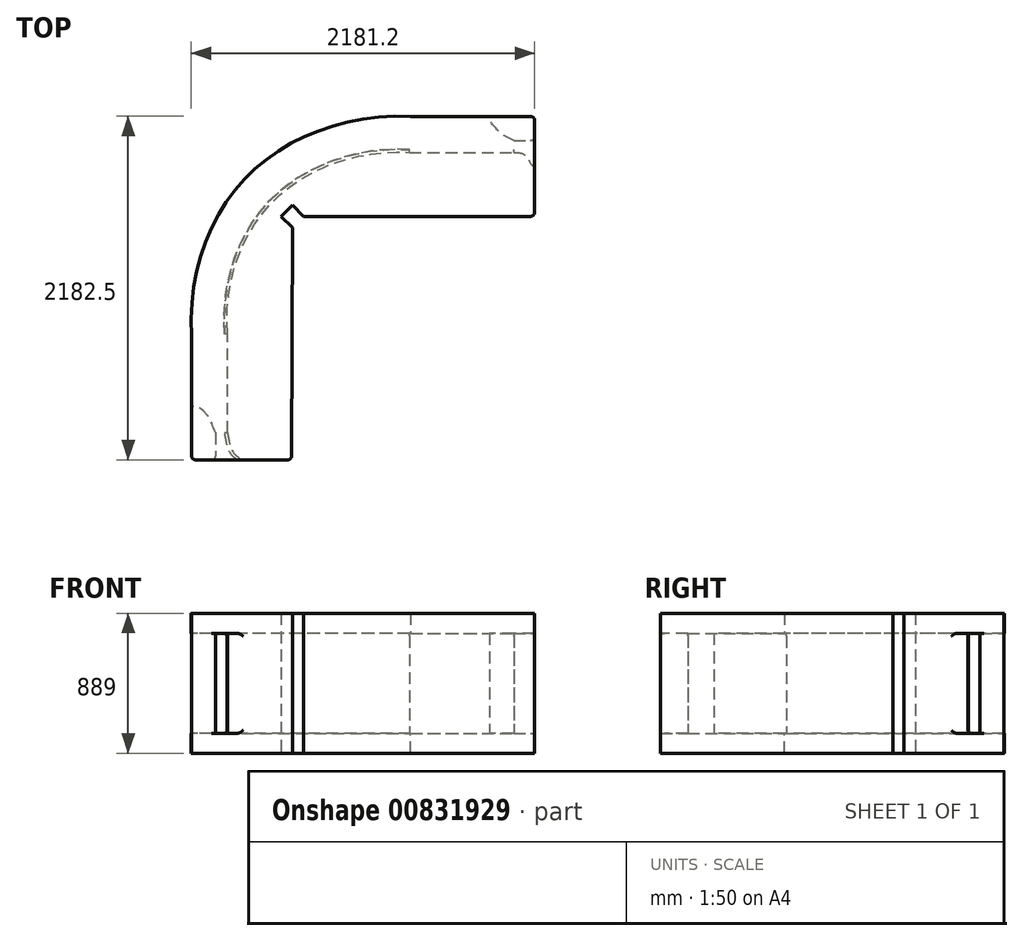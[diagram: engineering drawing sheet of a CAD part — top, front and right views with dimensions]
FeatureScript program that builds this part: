
annotation { "Feature Type Name" : "Feature", "Feature Type Description" : "" }
export const myFeature = defineFeature(function(context is Context, id is Id, definition is map)
    precondition{}
    {
        {
            var Q0;
            Q0=qCreatedBy(makeId("Top.planeOp"),FACE);
            var sketch = newSketch(context, id + "F0", { "sketchPlane" : qUnion([Q0])});
            skFitSpline(sketch, "E0", {"points": [v(690.67, 695.24) * mm, v(-328.68, 333.13) * mm, v(-700.43, -698.84) * mm], "startDerivative": vector(-2366.76, 83.62) * mm, "endDerivative": vector(144.45, -2458.95) * mm});
            skLineSegment(sketch, "E1.top", {"start": v(-700.43, -1486.24) * mm, "end": v(-548.3, -1486.24) * mm});
            skLineSegment(sketch, "E1.left", {"start": v(-700.43, -698.84) * mm, "end": v(-700.43, -1486.24) * mm});
            skLineSegment(sketch, "E2", {"start": v(690.67, 695.24) * mm, "end": v(1478.07, 695.24) * mm});
            skLineSegment(sketch, "E3", {"start": v(1478.07, 695.24) * mm, "end": v(1478.07, 542.84) * mm});
            skLineSegment(sketch, "E4", {"start": v(1478.07, 60.24) * mm, "end": v(11.22, 60.24) * mm});
            skLineSegment(sketch, "E5", {"start": v(11.22, 60.24) * mm, "end": v(-60.63, 132.08) * mm});
            skLineSegment(sketch, "E6", {"start": v(-60.63, 132.08) * mm, "end": v(-132.47, 60.24) * mm});
            skLineSegment(sketch, "E7", {"start": v(-132.47, 60.24) * mm, "end": v(-60.63, -11.6) * mm});
            skFitSpline(sketch, "E8.0", {"points": [v(685.29, 542.94) * mm, v(640.55, 544.52) * mm, v(551.83, 543.62) * mm, v(422.12, 530.41) * mm, v(296.88, 505.7) * mm, v(177.19, 469.84) * mm, v(82.92, 431.02) * mm, v(11.29, 394.8) * mm, v(-40.43, 365.12) * mm, v(-90.04, 332.94) * mm, v(-129.54, 304.1) * mm, v(-159.98, 279.84) * mm, v(-182.21, 261.04) * mm, v(-200.24, 244.9) * mm, v(-214.36, 231.68) * mm, v(-224.8, 221.62) * mm, v(-235.08, 211.4) * mm, v(-248.6, 197.59) * mm, v(-265.13, 179.92) * mm, v(-284.39, 158.12) * mm, v(-309.26, 128.25) * mm, v(-338.84, 89.45) * mm, v(-371.85, 40.62) * mm, v(-402.33, -10.4) * mm, v(-439.47, -81.22) * mm, v(-479.2, -174.78) * mm, v(-515.55, -294.36) * mm, v(-539.97, -420.49) * mm, v(-551.86, -552.38) * mm, v(-551.01, -643.6) * mm, v(-548.3, -689.9) * mm]});
            skPoint(sketch, "E9.end.orphan", {"position": v(1478.07, 542.84) * mm});
            skLineSegment(sketch, "E10", {"start": v(685.28, 542.94) * mm, "end": v(1478.07, 542.84) * mm});
            skLineSegment(sketch, "E11", {"start": v(-548.3, -689.9) * mm, "end": v(-548.3, -1486.24) * mm});
            skFitSpline(sketch, "E12.0", {"points": [v(682.6, 466.78) * mm, v(640.14, 468.28) * mm, v(556.03, 467.43) * mm, v(433.32, 454.93) * mm, v(315.16, 431.6) * mm, v(202.62, 397.88) * mm, v(114.33, 361.5) * mm, v(47.46, 327.7) * mm, v(-0.72, 300.04) * mm, v(-46.83, 270.14) * mm, v(-83.45, 243.4) * mm, v(-111.62, 220.93) * mm, v(-132.19, 203.55) * mm, v(-148.85, 188.63) * mm, v(-161.88, 176.43) * mm, v(-171.5, 167.15) * mm, v(-181, 157.73) * mm, v(-193.48, 144.97) * mm, v(-208.74, 128.66) * mm, v(-226.53, 108.51) * mm, v(-249.53, 80.9) * mm, v(-276.9, 44.98) * mm, v(-307.51, -0.28) * mm, v(-335.8, -47.65) * mm, v(-370.36, -113.52) * mm, v(-407.4, -200.76) * mm, v(-441.44, -312.66) * mm, v(-464.38, -431.1) * mm, v(-475.6, -555.36) * mm, v(-474.8, -641.6) * mm, v(-472.22, -685.44) * mm]});
            skFitSpline(sketch, "E13", {"points": [v(-382.93, -1486.24) * mm, v(-440.74, -1431.1) * mm, v(-472.22, -1313.71) * mm], "startDerivative": vector(-145.25, 103.15) * mm, "endDerivative": vector(-37.1, 237.24) * mm});
            skFitSpline(sketch, "E14", {"points": [v(1478.07, 377.74) * mm, v(1458.25, 389.6) * mm, v(1414.77, 449.69) * mm, v(1345.73, 466.64) * mm], "startDerivative": vector(-89.57, 29.33) * mm, "endDerivative": vector(-195.65, 6.2) * mm});
            skFitSpline(sketch, "E15", {"points": [v(-548.3, -1313.71) * mm, v(-592, -1216.08) * mm, v(-611.19, -1191.79) * mm, v(-646.99, -1158.54) * mm, v(-700.43, -1148.32) * mm], "startDerivative": vector(-138.78, 340.8) * mm, "endDerivative": vector(-232.68, 10.72) * mm});
            skFitSpline(sketch, "E16", {"points": [v(1345.73, 542.86) * mm, v(1261.3, 587.93) * mm, v(1234.52, 616.76) * mm, v(1195.4, 666.18) * mm, v(1190.25, 695.24) * mm], "startDerivative": vector(-299.2, 139.95) * mm, "endDerivative": vector(1.05, 148.57) * mm});
            skLineSegment(sketch, "E17", {"start": v(-65.43, -1486.24) * mm, "end": v(-60.63, -11.6) * mm});
            skLineSegment(sketch, "E18.trimOffspring", {"start": v(-382.93, -1486.24) * mm, "end": v(-65.43, -1486.24) * mm});
            skLineSegment(sketch, "E19.trimOffspring", {"start": v(1478.07, 377.74) * mm, "end": v(1478.07, 60.24) * mm});
            skLineSegment(sketch, "E20", {"start": v(-472.22, -1313.71) * mm, "end": v(-472.22, -685.44) * mm});
            skLineSegment(sketch, "E21", {"start": v(682.6, 466.79) * mm, "end": v(1345.73, 466.64) * mm});
            skLineSegment(sketch, "E22", {"start": v(-65.43, -1486.24) * mm, "end": v(-700.43, -1486.24) * mm});
            skLineSegment(sketch, "E23", {"start": v(-132.47, 60.24) * mm, "end": v(-60.63, 132.08) * mm});
            skLineSegment(sketch, "E24", {"start": v(11.22, 60.24) * mm, "end": v(1478.07, 60.24) * mm});
            skLineSegment(sketch, "E25", {"start": v(1478.07, 695.24) * mm, "end": v(690.67, 695.24) * mm});
            skFitSpline(sketch, "E26", {"points": [v(690.67, 695.24) * mm, v(-328.68, 333.13) * mm, v(-700.43, -698.84) * mm], "startDerivative": vector(-2366.76, 83.62) * mm, "endDerivative": vector(144.45, -2458.95) * mm});
            skLineSegment(sketch, "E27", {"start": v(1478.07, 60.24) * mm, "end": v(1478.07, 695.24) * mm});
            skSolve(sketch);
        }
        {
            var Q0;
            {var subQ0=sQuery(id+"F0.wireOp",EDGE,"E1.top");Q0=makeQuery(id+"F0.imprint","IMPRINT",FACE,{"disambiguationData":[TD([[makeQuery(id+"F0.imprint","IMPRINT",EDGE,{"derivedFrom":subQ0}),1.0]])]});}
            var Q1;
            {var subQ0=sQuery(id+"F0.wireOp",EDGE,"E3");Q1=makeQuery(id+"F0.imprint","IMPRINT",FACE,{"disambiguationData":[TD([[makeQuery(id+"F0.imprint","IMPRINT",EDGE,{"derivedFrom":subQ0}),-1.0]])]});}
            var Q2;
            Q2=makeQuery(id+"F0.imprint","IMPRINT",FACE,{"disambiguationData":[TD([[makeQuery(id+"F0.imprint","IMPRINT",EDGE,{"derivedFrom":sQuery(id+"F0.wireOp",EDGE,"E4")}),-1.0]])]});
            extrude(context, id + "F1", {"entities" : qUnion([Q0, Q1, Q2]), "endBound" : BoundingType.SYMMETRIC, "depth" : 889 * mm, "offsetDistance" : 25.4 * mm});
        }
        {
            var Q0;
            {var subQ5=sQuery(id+"F0.wireOp",EDGE,"E1.top");var subQ9=sQuery(id+"F0.wireOp",EDGE,"E8.0");var subQ10=makeQuery(id+"F0.imprint","IMPRINT",EDGE,{"derivedFrom":subQ9});var subQ17=sQuery(id+"F0.wireOp",EDGE,"E3");var subQ21=sQuery(id+"F0.wireOp",EDGE,"E0");Q0=qUnion([makeQuery(id+"F0.imprint","IMPRINT",FACE,{"disambiguationData":[TD([[makeQuery(id+"F0.imprint","IMPRINT",EDGE,{"derivedFrom":sQuery(id+"F0.wireOp",EDGE,"E4")}),-1.0]])]}),makeQuery(id+"F0.imprint","IMPRINT",FACE,{"disambiguationData":[TD([[makeQuery(id+"F0.imprint","IMPRINT",EDGE,{"derivedFrom":subQ5}),1.0]])]}),makeQuery(id+"F0.imprint","IMPRINT",FACE,{"disambiguationData":[TD([[makeQuery(id+"F0.imprint","IMPRINT",EDGE,{"derivedFrom":subQ17}),-1.0]])]}),makeQuery(id+"F0.imprint","IMPRINT",FACE,{"disambiguationData":[TD([[makeQuery(id+"F0.imprint","IMPRINT",EDGE,{"derivedFrom":subQ21}),1.0]])]}),makeQuery(id+"F0.imprint","IMPRINT",FACE,{"disambiguationData":[TD([[subQ10,1.0]])]})]);}
            var Q1;
            Q1=makeQuery(id+"F1.opExtrude","CAP_FACE",FACE,{"disambiguationData":[OSD([sQuery(id+"F0.wireOp",EDGE,"E4"),sQuery(id+"F0.wireOp",EDGE,"E5"),sQuery(id+"F0.wireOp",EDGE,"E6"),sQuery(id+"F0.wireOp",EDGE,"E7"),sQuery(id+"F0.wireOp",EDGE,"E12.0"),sQuery(id+"F0.wireOp",EDGE,"E13"),sQuery(id+"F0.wireOp",EDGE,"E14"),sQuery(id+"F0.wireOp",EDGE,"E17"),sQuery(id+"F0.wireOp",EDGE,"E18.trimOffspring"),sQuery(id+"F0.wireOp",EDGE,"E19.trimOffspring"),sQuery(id+"F0.wireOp",EDGE,"E20"),sQuery(id+"F0.wireOp",EDGE,"E21")])],"isStart":true});
            extrude(context, id + "F2", {"entities" : qUnion([Q0]), "endBound" : BoundingType.UP_TO_SURFACE, "oppositeDirection" : true, "depth" : 25.4 * mm, "endBoundEntityFace" : qUnion([Q1]), "hasOffset" : true, "offsetDistance" : 0 * mm, "hasSecondDirection" : true, "secondDirectionOppositeDirection" : false, "secondDirectionDepth" : -317.5 * mm});
        }
        {
            var Q0;
            {var subQ5=sQuery(id+"F0.wireOp",EDGE,"E1.top");var subQ9=sQuery(id+"F0.wireOp",EDGE,"E8.0");var subQ10=makeQuery(id+"F0.imprint","IMPRINT",EDGE,{"derivedFrom":subQ9});var subQ17=sQuery(id+"F0.wireOp",EDGE,"E3");var subQ21=sQuery(id+"F0.wireOp",EDGE,"E0");Q0=qUnion([makeQuery(id+"F0.imprint","IMPRINT",FACE,{"disambiguationData":[TD([[makeQuery(id+"F0.imprint","IMPRINT",EDGE,{"derivedFrom":sQuery(id+"F0.wireOp",EDGE,"E4")}),-1.0]])]}),makeQuery(id+"F0.imprint","IMPRINT",FACE,{"disambiguationData":[TD([[makeQuery(id+"F0.imprint","IMPRINT",EDGE,{"derivedFrom":subQ5}),1.0]])]}),makeQuery(id+"F0.imprint","IMPRINT",FACE,{"disambiguationData":[TD([[makeQuery(id+"F0.imprint","IMPRINT",EDGE,{"derivedFrom":subQ17}),-1.0]])]}),makeQuery(id+"F0.imprint","IMPRINT",FACE,{"disambiguationData":[TD([[makeQuery(id+"F0.imprint","IMPRINT",EDGE,{"derivedFrom":subQ21}),1.0]])]}),makeQuery(id+"F0.imprint","IMPRINT",FACE,{"disambiguationData":[TD([[subQ10,1.0]])]})]);}
            var Q1;
            Q1=makeQuery(id+"F1.opExtrude","CAP_FACE",FACE,{"disambiguationData":[OSD([sQuery(id+"F0.wireOp",EDGE,"E4"),sQuery(id+"F0.wireOp",EDGE,"E5"),sQuery(id+"F0.wireOp",EDGE,"E6"),sQuery(id+"F0.wireOp",EDGE,"E7"),sQuery(id+"F0.wireOp",EDGE,"E12.0"),sQuery(id+"F0.wireOp",EDGE,"E13"),sQuery(id+"F0.wireOp",EDGE,"E14"),sQuery(id+"F0.wireOp",EDGE,"E17"),sQuery(id+"F0.wireOp",EDGE,"E18.trimOffspring"),sQuery(id+"F0.wireOp",EDGE,"E19.trimOffspring"),sQuery(id+"F0.wireOp",EDGE,"E20"),sQuery(id+"F0.wireOp",EDGE,"E21")])],"isStart":false});
            extrude(context, id + "F3", {"entities" : qUnion([Q0]), "endBound" : BoundingType.UP_TO_SURFACE, "depth" : 25.4 * mm, "endBoundEntityFace" : qUnion([Q1]), "offsetDistance" : 25.4 * mm, "hasSecondDirection" : true, "secondDirectionOppositeDirection" : true, "secondDirectionDepth" : -317.5 * mm});
        }
        {
            var Q0;
            Q0=makeQuery(id+"F1.opExtrude","SWEPT_BODY",BODY,{"disambiguationData":[OSD([sQuery(id+"F0.wireOp",EDGE,"E1.top"),sQuery(id+"F0.wireOp",EDGE,"E1.left"),sQuery(id+"F0.wireOp",EDGE,"E11"),sQuery(id+"F0.wireOp",EDGE,"E15")])]});
            var Q1;
            Q1=makeQuery(id+"F1.opExtrude","SWEPT_BODY",BODY,{"disambiguationData":[OSD([sQuery(id+"F0.wireOp",EDGE,"E4"),sQuery(id+"F0.wireOp",EDGE,"E5"),sQuery(id+"F0.wireOp",EDGE,"E6"),sQuery(id+"F0.wireOp",EDGE,"E7"),sQuery(id+"F0.wireOp",EDGE,"E12.0"),sQuery(id+"F0.wireOp",EDGE,"E13"),sQuery(id+"F0.wireOp",EDGE,"E14"),sQuery(id+"F0.wireOp",EDGE,"E17"),sQuery(id+"F0.wireOp",EDGE,"E18.trimOffspring"),sQuery(id+"F0.wireOp",EDGE,"E19.trimOffspring"),sQuery(id+"F0.wireOp",EDGE,"E20"),sQuery(id+"F0.wireOp",EDGE,"E21")])]});
            var Q2;
            Q2=makeQuery(id+"F1.opExtrude","SWEPT_BODY",BODY,{"disambiguationData":[OSD([sQuery(id+"F0.wireOp",EDGE,"E2"),sQuery(id+"F0.wireOp",EDGE,"E3"),sQuery(id+"F0.wireOp",EDGE,"E10"),sQuery(id+"F0.wireOp",EDGE,"E16")])]});
            var Q3;
            Q3=makeQuery(id+"F2.opExtrude","SWEPT_BODY",BODY,{"disambiguationData":[OSD([sQuery(id+"F0.wireOp",EDGE,"E0"),sQuery(id+"F0.wireOp",EDGE,"E1.top"),sQuery(id+"F0.wireOp",EDGE,"E1.left"),sQuery(id+"F0.wireOp",EDGE,"E2"),sQuery(id+"F0.wireOp",EDGE,"E3"),sQuery(id+"F0.wireOp",EDGE,"E4"),sQuery(id+"F0.wireOp",EDGE,"E5"),sQuery(id+"F0.wireOp",EDGE,"E6"),sQuery(id+"F0.wireOp",EDGE,"E7"),sQuery(id+"F0.wireOp",EDGE,"E17"),sQuery(id+"F0.wireOp",EDGE,"E18.trimOffspring"),sQuery(id+"F0.wireOp",EDGE,"E19.trimOffspring"),sQuery(id+"F0.wireOp",EDGE,"E22"),sQuery(id+"F0.wireOp",EDGE,"E27")])]});
            var Q4;
            Q4=makeQuery(id+"F3.opExtrude","SWEPT_BODY",BODY,{"disambiguationData":[OSD([sQuery(id+"F0.wireOp",EDGE,"E0"),sQuery(id+"F0.wireOp",EDGE,"E1.top"),sQuery(id+"F0.wireOp",EDGE,"E1.left"),sQuery(id+"F0.wireOp",EDGE,"E2"),sQuery(id+"F0.wireOp",EDGE,"E3"),sQuery(id+"F0.wireOp",EDGE,"E4"),sQuery(id+"F0.wireOp",EDGE,"E5"),sQuery(id+"F0.wireOp",EDGE,"E6"),sQuery(id+"F0.wireOp",EDGE,"E7"),sQuery(id+"F0.wireOp",EDGE,"E17"),sQuery(id+"F0.wireOp",EDGE,"E18.trimOffspring"),sQuery(id+"F0.wireOp",EDGE,"E19.trimOffspring"),sQuery(id+"F0.wireOp",EDGE,"E22"),sQuery(id+"F0.wireOp",EDGE,"E27")])]});
            booleanBodies(context, id + "F4", {"operationType" : BooleanOperationType.UNION, "tools" : qUnion([Q0, Q1, Q2, Q3, Q4])});
        }
        {
            var Q0;
            Q0=makeQuery(id+"F1.opExtrude","SWEPT_EDGE",EDGE,{"disambiguationData":[OSD([sQuery(id+"F0.wireOp",EDGE,"E2"),sQuery(id+"F0.wireOp",EDGE,"E3")])]});
            var Q1;
            Q1=makeQuery(id+"F1.opExtrude","SWEPT_EDGE",EDGE,{"disambiguationData":[OSD([sQuery(id+"F0.wireOp",EDGE,"E3"),sQuery(id+"F0.wireOp",EDGE,"E10"),sQuery(id+"F0.wireOp",EDGE,"E27")])]});
            var Q2;
            Q2=makeQuery(id+"F1.opExtrude","SWEPT_EDGE",EDGE,{"disambiguationData":[OSD([sQuery(id+"F0.wireOp",EDGE,"E1.top"),sQuery(id+"F0.wireOp",EDGE,"E11"),sQuery(id+"F0.wireOp",EDGE,"E22")])]});
            var Q3;
            Q3=makeQuery(id+"F1.opExtrude","SWEPT_EDGE",EDGE,{"disambiguationData":[OSD([sQuery(id+"F0.wireOp",EDGE,"E1.top"),sQuery(id+"F0.wireOp",EDGE,"E1.left")])]});
            var Q4;
            Q4=makeQuery(id+"F1.opExtrude","SWEPT_EDGE",EDGE,{"disambiguationData":[OSD([sQuery(id+"F0.wireOp",EDGE,"E4"),sQuery(id+"F0.wireOp",EDGE,"E19.trimOffspring")])]});
            var Q5;
            Q5=makeQuery(id+"F1.opExtrude","SWEPT_EDGE",EDGE,{"disambiguationData":[OSD([sQuery(id+"F0.wireOp",EDGE,"E17"),sQuery(id+"F0.wireOp",EDGE,"E18.trimOffspring")])]});
            var Q6;
            Q6=makeQuery(id+"F1.opExtrude","SWEPT_EDGE",EDGE,{"disambiguationData":[OSD([sQuery(id+"F0.wireOp",EDGE,"E14"),sQuery(id+"F0.wireOp",EDGE,"E19.trimOffspring"),sQuery(id+"F0.wireOp",EDGE,"E27")])]});
            var Q7;
            Q7=makeQuery(id+"F1.opExtrude","SWEPT_EDGE",EDGE,{"disambiguationData":[OSD([sQuery(id+"F0.wireOp",EDGE,"E13"),sQuery(id+"F0.wireOp",EDGE,"E18.trimOffspring"),sQuery(id+"F0.wireOp",EDGE,"E22")])]});
            fillet(context, id + "F5", {"entities" : qUnion([Q0, Q1, Q2, Q3, Q4, Q5, Q6, Q7]), "radius" : 25.4 * mm, "tangentPropagation" : true, "allowEdgeOverflow" : false});
        }
        {
            var Q0;
            Q0=makeQuery(id+"F4.opBoolean","INTERSECT",EDGE,{"derivedFrom":[makeQuery(id+"F1.opExtrude","SWEPT_FACE",FACE,{"disambiguationData":[OSD([sQuery(id+"F0.wireOp",EDGE,"E21")])]}),makeQuery(id+"F3.opExtrude","CAP_FACE",FACE,{"disambiguationData":[OSD([sQuery(id+"F0.wireOp",EDGE,"E0"),sQuery(id+"F0.wireOp",EDGE,"E1.top"),sQuery(id+"F0.wireOp",EDGE,"E1.left"),sQuery(id+"F0.wireOp",EDGE,"E2"),sQuery(id+"F0.wireOp",EDGE,"E3"),sQuery(id+"F0.wireOp",EDGE,"E4"),sQuery(id+"F0.wireOp",EDGE,"E5"),sQuery(id+"F0.wireOp",EDGE,"E6"),sQuery(id+"F0.wireOp",EDGE,"E7"),sQuery(id+"F0.wireOp",EDGE,"E17"),sQuery(id+"F0.wireOp",EDGE,"E18.trimOffspring"),sQuery(id+"F0.wireOp",EDGE,"E19.trimOffspring"),sQuery(id+"F0.wireOp",EDGE,"E22"),sQuery(id+"F0.wireOp",EDGE,"E27")])],"isStart":true})]});
            var Q1;
            Q1=makeQuery(id+"F4.opBoolean","INTERSECT",EDGE,{"derivedFrom":[makeQuery(id+"F1.opExtrude","SWEPT_FACE",FACE,{"disambiguationData":[OSD([sQuery(id+"F0.wireOp",EDGE,"E12.0")])]}),makeQuery(id+"F3.opExtrude","CAP_FACE",FACE,{"disambiguationData":[OSD([sQuery(id+"F0.wireOp",EDGE,"E0"),sQuery(id+"F0.wireOp",EDGE,"E1.top"),sQuery(id+"F0.wireOp",EDGE,"E1.left"),sQuery(id+"F0.wireOp",EDGE,"E2"),sQuery(id+"F0.wireOp",EDGE,"E3"),sQuery(id+"F0.wireOp",EDGE,"E4"),sQuery(id+"F0.wireOp",EDGE,"E5"),sQuery(id+"F0.wireOp",EDGE,"E6"),sQuery(id+"F0.wireOp",EDGE,"E7"),sQuery(id+"F0.wireOp",EDGE,"E17"),sQuery(id+"F0.wireOp",EDGE,"E18.trimOffspring"),sQuery(id+"F0.wireOp",EDGE,"E19.trimOffspring"),sQuery(id+"F0.wireOp",EDGE,"E22"),sQuery(id+"F0.wireOp",EDGE,"E27")])],"isStart":true})]});
            var Q2;
            Q2=makeQuery(id+"F4.opBoolean","INTERSECT",EDGE,{"derivedFrom":[makeQuery(id+"F1.opExtrude","SWEPT_FACE",FACE,{"disambiguationData":[OSD([sQuery(id+"F0.wireOp",EDGE,"E20")])]}),makeQuery(id+"F3.opExtrude","CAP_FACE",FACE,{"disambiguationData":[OSD([sQuery(id+"F0.wireOp",EDGE,"E0"),sQuery(id+"F0.wireOp",EDGE,"E1.top"),sQuery(id+"F0.wireOp",EDGE,"E1.left"),sQuery(id+"F0.wireOp",EDGE,"E2"),sQuery(id+"F0.wireOp",EDGE,"E3"),sQuery(id+"F0.wireOp",EDGE,"E4"),sQuery(id+"F0.wireOp",EDGE,"E5"),sQuery(id+"F0.wireOp",EDGE,"E6"),sQuery(id+"F0.wireOp",EDGE,"E7"),sQuery(id+"F0.wireOp",EDGE,"E17"),sQuery(id+"F0.wireOp",EDGE,"E18.trimOffspring"),sQuery(id+"F0.wireOp",EDGE,"E19.trimOffspring"),sQuery(id+"F0.wireOp",EDGE,"E22"),sQuery(id+"F0.wireOp",EDGE,"E27")])],"isStart":true})]});
            var Q3;
            Q3=makeQuery(id+"F4.opBoolean","INTERSECT",EDGE,{"derivedFrom":[makeQuery(id+"F1.opExtrude","SWEPT_FACE",FACE,{"disambiguationData":[OSD([sQuery(id+"F0.wireOp",EDGE,"E13")])]}),makeQuery(id+"F3.opExtrude","CAP_FACE",FACE,{"disambiguationData":[OSD([sQuery(id+"F0.wireOp",EDGE,"E0"),sQuery(id+"F0.wireOp",EDGE,"E1.top"),sQuery(id+"F0.wireOp",EDGE,"E1.left"),sQuery(id+"F0.wireOp",EDGE,"E2"),sQuery(id+"F0.wireOp",EDGE,"E3"),sQuery(id+"F0.wireOp",EDGE,"E4"),sQuery(id+"F0.wireOp",EDGE,"E5"),sQuery(id+"F0.wireOp",EDGE,"E6"),sQuery(id+"F0.wireOp",EDGE,"E7"),sQuery(id+"F0.wireOp",EDGE,"E17"),sQuery(id+"F0.wireOp",EDGE,"E18.trimOffspring"),sQuery(id+"F0.wireOp",EDGE,"E19.trimOffspring"),sQuery(id+"F0.wireOp",EDGE,"E22"),sQuery(id+"F0.wireOp",EDGE,"E27")])],"isStart":true})]});
            var Q4;
            Q4=makeQuery(id+"F4.opBoolean","INTERSECT",EDGE,{"derivedFrom":[makeQuery(id+"F1.opExtrude","SWEPT_FACE",FACE,{"disambiguationData":[OSD([sQuery(id+"F0.wireOp",EDGE,"E14")])]}),makeQuery(id+"F3.opExtrude","CAP_FACE",FACE,{"disambiguationData":[OSD([sQuery(id+"F0.wireOp",EDGE,"E0"),sQuery(id+"F0.wireOp",EDGE,"E1.top"),sQuery(id+"F0.wireOp",EDGE,"E1.left"),sQuery(id+"F0.wireOp",EDGE,"E2"),sQuery(id+"F0.wireOp",EDGE,"E3"),sQuery(id+"F0.wireOp",EDGE,"E4"),sQuery(id+"F0.wireOp",EDGE,"E5"),sQuery(id+"F0.wireOp",EDGE,"E6"),sQuery(id+"F0.wireOp",EDGE,"E7"),sQuery(id+"F0.wireOp",EDGE,"E17"),sQuery(id+"F0.wireOp",EDGE,"E18.trimOffspring"),sQuery(id+"F0.wireOp",EDGE,"E19.trimOffspring"),sQuery(id+"F0.wireOp",EDGE,"E22"),sQuery(id+"F0.wireOp",EDGE,"E27")])],"isStart":true})]});
            var Q5;
            Q5=makeQuery(id+"F4.opBoolean","INTERSECT",EDGE,{"derivedFrom":[makeQuery(id+"F1.opExtrude","SWEPT_FACE",FACE,{"disambiguationData":[OSD([sQuery(id+"F0.wireOp",EDGE,"E14")])]}),makeQuery(id+"F2.opExtrude","CAP_FACE",FACE,{"disambiguationData":[OSD([sQuery(id+"F0.wireOp",EDGE,"E0"),sQuery(id+"F0.wireOp",EDGE,"E1.top"),sQuery(id+"F0.wireOp",EDGE,"E1.left"),sQuery(id+"F0.wireOp",EDGE,"E2"),sQuery(id+"F0.wireOp",EDGE,"E3"),sQuery(id+"F0.wireOp",EDGE,"E4"),sQuery(id+"F0.wireOp",EDGE,"E5"),sQuery(id+"F0.wireOp",EDGE,"E6"),sQuery(id+"F0.wireOp",EDGE,"E7"),sQuery(id+"F0.wireOp",EDGE,"E17"),sQuery(id+"F0.wireOp",EDGE,"E18.trimOffspring"),sQuery(id+"F0.wireOp",EDGE,"E19.trimOffspring"),sQuery(id+"F0.wireOp",EDGE,"E22"),sQuery(id+"F0.wireOp",EDGE,"E27")])],"isStart":true})]});
            var Q6;
            Q6=makeQuery(id+"F4.opBoolean","INTERSECT",EDGE,{"derivedFrom":[makeQuery(id+"F1.opExtrude","SWEPT_FACE",FACE,{"disambiguationData":[OSD([sQuery(id+"F0.wireOp",EDGE,"E21")])]}),makeQuery(id+"F2.opExtrude","CAP_FACE",FACE,{"disambiguationData":[OSD([sQuery(id+"F0.wireOp",EDGE,"E0"),sQuery(id+"F0.wireOp",EDGE,"E1.top"),sQuery(id+"F0.wireOp",EDGE,"E1.left"),sQuery(id+"F0.wireOp",EDGE,"E2"),sQuery(id+"F0.wireOp",EDGE,"E3"),sQuery(id+"F0.wireOp",EDGE,"E4"),sQuery(id+"F0.wireOp",EDGE,"E5"),sQuery(id+"F0.wireOp",EDGE,"E6"),sQuery(id+"F0.wireOp",EDGE,"E7"),sQuery(id+"F0.wireOp",EDGE,"E17"),sQuery(id+"F0.wireOp",EDGE,"E18.trimOffspring"),sQuery(id+"F0.wireOp",EDGE,"E19.trimOffspring"),sQuery(id+"F0.wireOp",EDGE,"E22"),sQuery(id+"F0.wireOp",EDGE,"E27")])],"isStart":true})]});
            var Q7;
            Q7=makeQuery(id+"F4.opBoolean","INTERSECT",EDGE,{"derivedFrom":[makeQuery(id+"F1.opExtrude","SWEPT_FACE",FACE,{"disambiguationData":[OSD([sQuery(id+"F0.wireOp",EDGE,"E12.0")])]}),makeQuery(id+"F2.opExtrude","CAP_FACE",FACE,{"disambiguationData":[OSD([sQuery(id+"F0.wireOp",EDGE,"E0"),sQuery(id+"F0.wireOp",EDGE,"E1.top"),sQuery(id+"F0.wireOp",EDGE,"E1.left"),sQuery(id+"F0.wireOp",EDGE,"E2"),sQuery(id+"F0.wireOp",EDGE,"E3"),sQuery(id+"F0.wireOp",EDGE,"E4"),sQuery(id+"F0.wireOp",EDGE,"E5"),sQuery(id+"F0.wireOp",EDGE,"E6"),sQuery(id+"F0.wireOp",EDGE,"E7"),sQuery(id+"F0.wireOp",EDGE,"E17"),sQuery(id+"F0.wireOp",EDGE,"E18.trimOffspring"),sQuery(id+"F0.wireOp",EDGE,"E19.trimOffspring"),sQuery(id+"F0.wireOp",EDGE,"E22"),sQuery(id+"F0.wireOp",EDGE,"E27")])],"isStart":true})]});
            var Q8;
            Q8=makeQuery(id+"F4.opBoolean","INTERSECT",EDGE,{"derivedFrom":[makeQuery(id+"F1.opExtrude","SWEPT_FACE",FACE,{"disambiguationData":[OSD([sQuery(id+"F0.wireOp",EDGE,"E20")])]}),makeQuery(id+"F2.opExtrude","CAP_FACE",FACE,{"disambiguationData":[OSD([sQuery(id+"F0.wireOp",EDGE,"E0"),sQuery(id+"F0.wireOp",EDGE,"E1.top"),sQuery(id+"F0.wireOp",EDGE,"E1.left"),sQuery(id+"F0.wireOp",EDGE,"E2"),sQuery(id+"F0.wireOp",EDGE,"E3"),sQuery(id+"F0.wireOp",EDGE,"E4"),sQuery(id+"F0.wireOp",EDGE,"E5"),sQuery(id+"F0.wireOp",EDGE,"E6"),sQuery(id+"F0.wireOp",EDGE,"E7"),sQuery(id+"F0.wireOp",EDGE,"E17"),sQuery(id+"F0.wireOp",EDGE,"E18.trimOffspring"),sQuery(id+"F0.wireOp",EDGE,"E19.trimOffspring"),sQuery(id+"F0.wireOp",EDGE,"E22"),sQuery(id+"F0.wireOp",EDGE,"E27")])],"isStart":true})]});
            var Q9;
            Q9=makeQuery(id+"F4.opBoolean","INTERSECT",EDGE,{"derivedFrom":[makeQuery(id+"F1.opExtrude","SWEPT_FACE",FACE,{"disambiguationData":[OSD([sQuery(id+"F0.wireOp",EDGE,"E13")])]}),makeQuery(id+"F2.opExtrude","CAP_FACE",FACE,{"disambiguationData":[OSD([sQuery(id+"F0.wireOp",EDGE,"E0"),sQuery(id+"F0.wireOp",EDGE,"E1.top"),sQuery(id+"F0.wireOp",EDGE,"E1.left"),sQuery(id+"F0.wireOp",EDGE,"E2"),sQuery(id+"F0.wireOp",EDGE,"E3"),sQuery(id+"F0.wireOp",EDGE,"E4"),sQuery(id+"F0.wireOp",EDGE,"E5"),sQuery(id+"F0.wireOp",EDGE,"E6"),sQuery(id+"F0.wireOp",EDGE,"E7"),sQuery(id+"F0.wireOp",EDGE,"E17"),sQuery(id+"F0.wireOp",EDGE,"E18.trimOffspring"),sQuery(id+"F0.wireOp",EDGE,"E19.trimOffspring"),sQuery(id+"F0.wireOp",EDGE,"E22"),sQuery(id+"F0.wireOp",EDGE,"E27")])],"isStart":true})]});
            fillet(context, id + "F6", {"entities" : qUnion([Q0, Q1, Q2, Q3, Q4, Q5, Q6, Q7, Q8, Q9]), "radius" : 17.78 * mm, "tangentPropagation" : true, "allowEdgeOverflow" : false});
        }
    });
